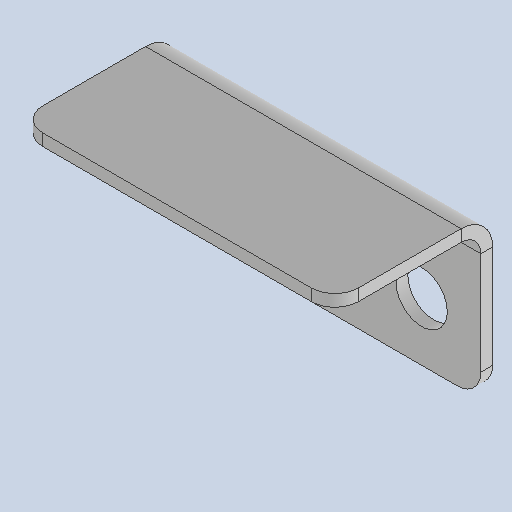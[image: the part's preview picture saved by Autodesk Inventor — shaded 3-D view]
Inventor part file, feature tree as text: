
AUTODESK INVENTOR PART (.ipt)
format: ipt  version: 2025 (Build 290162010, 162A)  size: 301,568 bytes
history: native  units: mm
features: sheet_metal_op x4, other x4, sketch x3, chamfer x1
ambient origin geometry x8: Origin, YZ Plane, XZ Plane, XY Plane, X Axis, Y Axis, Z Axis, Center Point
bodies: Body1 (feature_tree)
feature tree (12):
  sheet_metal_op  "Face2"
  sheet_metal_op  "Flange1"
  chamfer  "Corner Round6"
  sketch  "Sketch4"  dims[d36=80.0mm]
  other  "Plate2"
  sketch  "Sketch5"  dims[d37=40.0mm]
  sketch  "Sketch6"  dims[d38=3.0mm d39=50.0mm d40=15.0mm d41=13.0mm d42=3.0mm d43=0.0mm d44=3.0mm d45=1.5mm d46=6.0mm d47=5.0mm d48=40.0mm d49=90.0deg d50=5.0mm d51=12.0mm d52=3.0mm d53=5.0mm d54=6.0mm]
  other  "Plate3"
  sheet_metal_op  "Bend1"
  sheet_metal_op  "Corner1"
  other  "Cut1"
  other  "Definition1"
